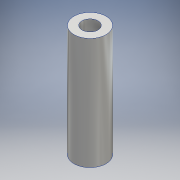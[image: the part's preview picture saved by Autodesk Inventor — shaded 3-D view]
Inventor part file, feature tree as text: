
AUTODESK INVENTOR PART (.ipt)
format: ipt  version: 2016 (Build 200138000, 138)  size: 108,032 bytes
history: native  units: mm
features: sketch x2, extrude x2, hole x2, other x1
ambient origin geometry x8: Origin, YZ Plane, XZ Plane, XY Plane, X Axis, Y Axis, Z Axis, Center Point
bodies: Body1 (feature_tree)
feature tree (7):
  other  "ソリッド1"
  sketch  "スケッチ1"
  extrude  "押し出し1"  Depth=6.0mm
  sketch  "スケッチ2"
  extrude  "押し出し2"  Depth=3.001mm
  hole  "穴1"  [1 undecoded]
  hole  "穴2"  [1 undecoded]
note: 2 required parameter values undecoded (feature->parameter linkage not recoverable at this tier; creation-order binding heuristic only, values carry confidence <= 0.55)
